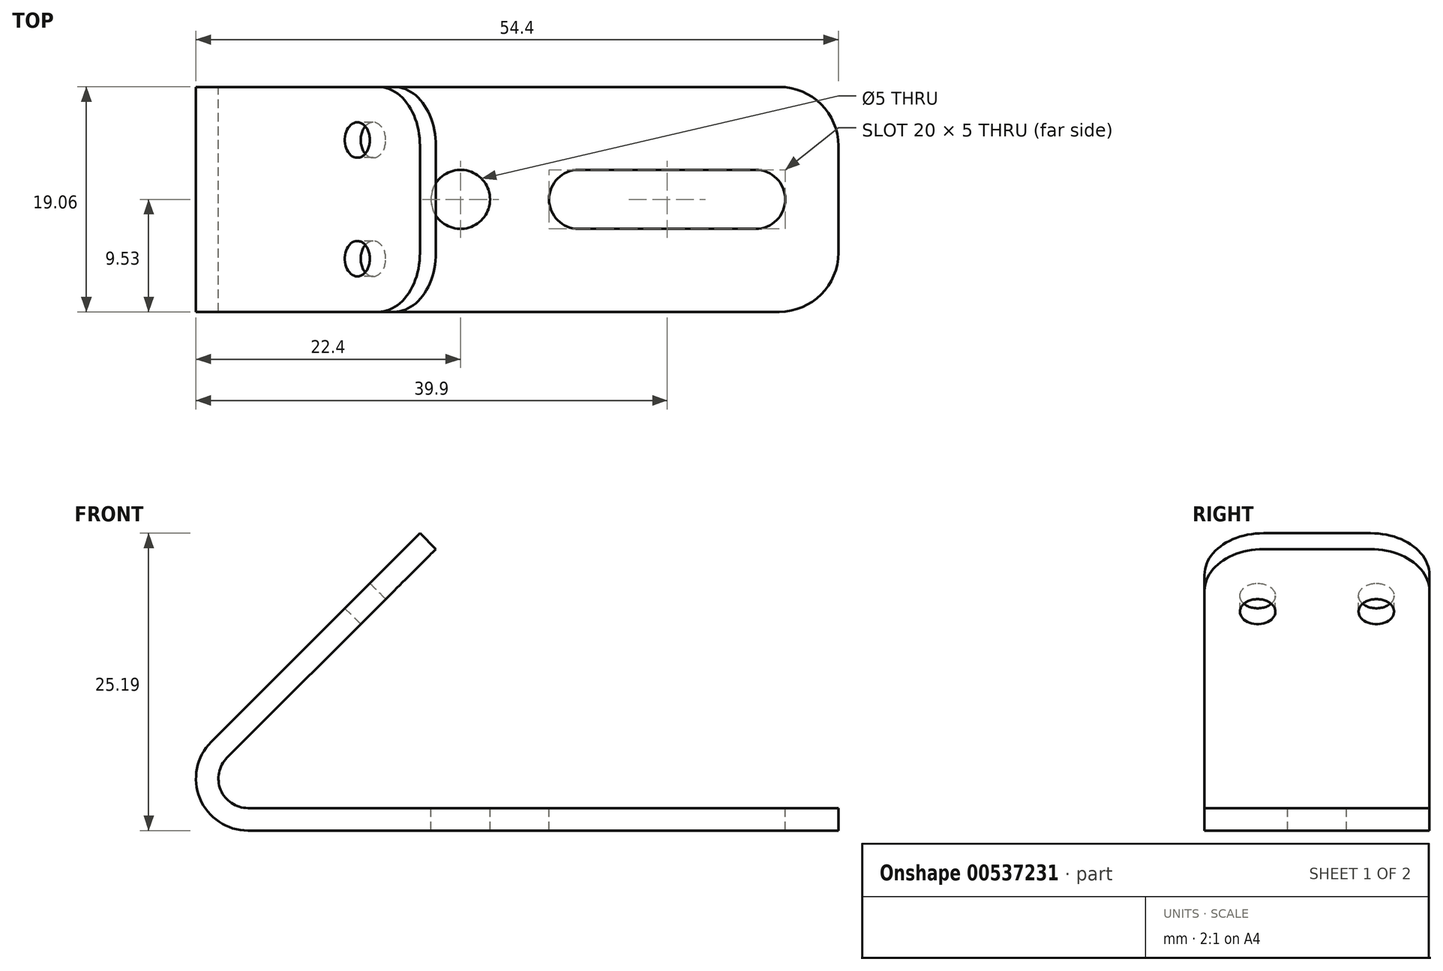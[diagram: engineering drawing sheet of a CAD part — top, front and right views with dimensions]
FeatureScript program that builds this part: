
annotation { "Feature Type Name" : "Feature", "Feature Type Description" : "" }
export const myFeature = defineFeature(function(context is Context, id is Id, definition is map)
    precondition{}
    {
        {
            var Q0;
            Q0=qCreatedBy(makeId("Front.planeOp"),FACE);
            var sketch = newSketch(context, id + "F0", { "sketchPlane" : qUnion([Q0])});
            skArc(sketch, "E0", {"start": v(-3.11, 3.11) * mm, "mid": v(-4.07, -1.68) * mm, "end": v(0, -4.4) * mm});
            skLineSegment(sketch, "E1", {"start": v(0, -4.4) * mm, "end": v(50, -4.4) * mm});
            skArc(sketch, "E2", {"start": v(-1.77, 1.77) * mm, "mid": v(-2.3, -0.96) * mm, "end": v(0, -2.5) * mm});
            skLineSegment(sketch, "E3", {"start": v(0, -2.5) * mm, "end": v(50, -2.5) * mm});
            skLineSegment(sketch, "E4", {"start": v(50, -4.4) * mm, "end": v(50, -2.5) * mm});
            skLineSegment(sketch, "E5", {"start": v(-3.11, 3.11) * mm, "end": v(14.57, 20.79) * mm});
            skLineSegment(sketch, "E6", {"start": v(-1.77, 1.77) * mm, "end": v(15.9, 19.45) * mm});
            skLineSegment(sketch, "E7", {"start": v(14.57, 20.79) * mm, "end": v(15.9, 19.45) * mm});
            skSolve(sketch);
        }
        {
            var Q0;
            Q0=makeQuery(id+"F0.imprint","IMPRINT",FACE,{"disambiguationData":[TD([[makeQuery(id+"F0.imprint","IMPRINT",EDGE,{"derivedFrom":sQuery(id+"F0.wireOp",EDGE,"E0")}),1.0]])]});
            extrude(context, id + "F1", {"entities" : qUnion([Q0]), "depth" : 19.05 * mm, "offsetDistance" : 25 * mm, "symmetric" : true});
        }
        {
            var Q0;
            Q0=makeQuery(id+"F1.opExtrude","SWEPT_FACE",FACE,{"disambiguationData":[OSD([sQuery(id+"F0.wireOp",EDGE,"E3")])]});
            var sketch = newSketch(context, id + "F2", { "sketchPlane" : qUnion([Q0])});
            skCircle(sketch, "E8", {"center": v(18, 0) * mm, "radius": 2.5 * mm});
            skArc(sketch, "E9", {"start": v(28, 2.5) * mm, "mid": v(25.5, 0) * mm, "end": v(28, -2.5) * mm});
            skArc(sketch, "E10", {"start": v(43, -2.5) * mm, "mid": v(45.5, 0) * mm, "end": v(43, 2.5) * mm});
            skLineSegment(sketch, "E11", {"start": v(28, 2.5) * mm, "end": v(43, 2.5) * mm});
            skLineSegment(sketch, "E12", {"start": v(28, -2.5) * mm, "end": v(43, -2.5) * mm});
            skSolve(sketch);
        }
        {
            var Q0;
            Q0=makeQuery(id+"F2.imprint","IMPRINT",FACE,{"disambiguationData":[TD([[makeQuery(id+"F2.imprint","IMPRINT",EDGE,{"derivedFrom":sQuery(id+"F2.wireOp",EDGE,"E9")}),1.0]])]});
            var Q1;
            Q1=makeQuery(id+"F2.imprint","IMPRINT",FACE,{"disambiguationData":[TD([[makeQuery(id+"F2.imprint","IMPRINT",EDGE,{"derivedFrom":sQuery(id+"F2.wireOp",EDGE,"E8")}),1.0]])]});
            extrude(context, id + "F3", {"entities" : qUnion([Q0, Q1]), "operationType" : NewBodyOperationType.REMOVE, "endBound" : BoundingType.THROUGH_ALL, "oppositeDirection" : true, "depth" : 25 * mm, "offsetDistance" : 25 * mm});
        }
        {
            var Q0;
            Q0=makeQuery(id+"F1.opExtrude","SWEPT_FACE",FACE,{"disambiguationData":[OSD([sQuery(id+"F0.wireOp",EDGE,"E5")])]});
            var sketch = newSketch(context, id + "F4", { "sketchPlane" : qUnion([Q0])});
            skCircle(sketch, "E13", {"center": v(-5.03, 17.5) * mm, "radius": 1.5 * mm});
            skCircle(sketch, "E14", {"center": v(5.03, 17.5) * mm, "radius": 1.5 * mm});
            skSolve(sketch);
        }
        {
            var Q0;
            Q0=makeQuery(id+"F4.imprint","IMPRINT",FACE,{"disambiguationData":[TD([[makeQuery(id+"F4.imprint","IMPRINT",EDGE,{"derivedFrom":sQuery(id+"F4.wireOp",EDGE,"E13")}),1.0]])]});
            var Q1;
            Q1=makeQuery(id+"F4.imprint","IMPRINT",FACE,{"disambiguationData":[TD([[makeQuery(id+"F4.imprint","IMPRINT",EDGE,{"derivedFrom":sQuery(id+"F4.wireOp",EDGE,"E14")}),1.0]])]});
            extrude(context, id + "F5", {"entities" : qUnion([Q0, Q1]), "operationType" : NewBodyOperationType.REMOVE, "oppositeDirection" : true, "depth" : 10 * mm, "offsetDistance" : 25 * mm});
        }
        {
            var Q0;
            Q0=makeQuery(id+"F1.opExtrude","CAP_EDGE",EDGE,{"disambiguationData":[OSD([sQuery(id+"F0.wireOp",EDGE,"E7")])],"isStart":true});
            var Q1;
            Q1=makeQuery(id+"F1.opExtrude","CAP_EDGE",EDGE,{"disambiguationData":[OSD([sQuery(id+"F0.wireOp",EDGE,"E4")])],"isStart":false});
            var Q2;
            Q2=makeQuery(id+"F1.opExtrude","CAP_EDGE",EDGE,{"disambiguationData":[OSD([sQuery(id+"F0.wireOp",EDGE,"E7")])],"isStart":false});
            var Q3;
            Q3=makeQuery(id+"F1.opExtrude","CAP_EDGE",EDGE,{"disambiguationData":[OSD([sQuery(id+"F0.wireOp",EDGE,"E4")])],"isStart":true});
            fillet(context, id + "F6", {"entities" : qUnion([Q0, Q1, Q2, Q3]), "radius" : 5 * mm, "tangentPropagation" : true, "allowEdgeOverflow" : false});
        }
    });
